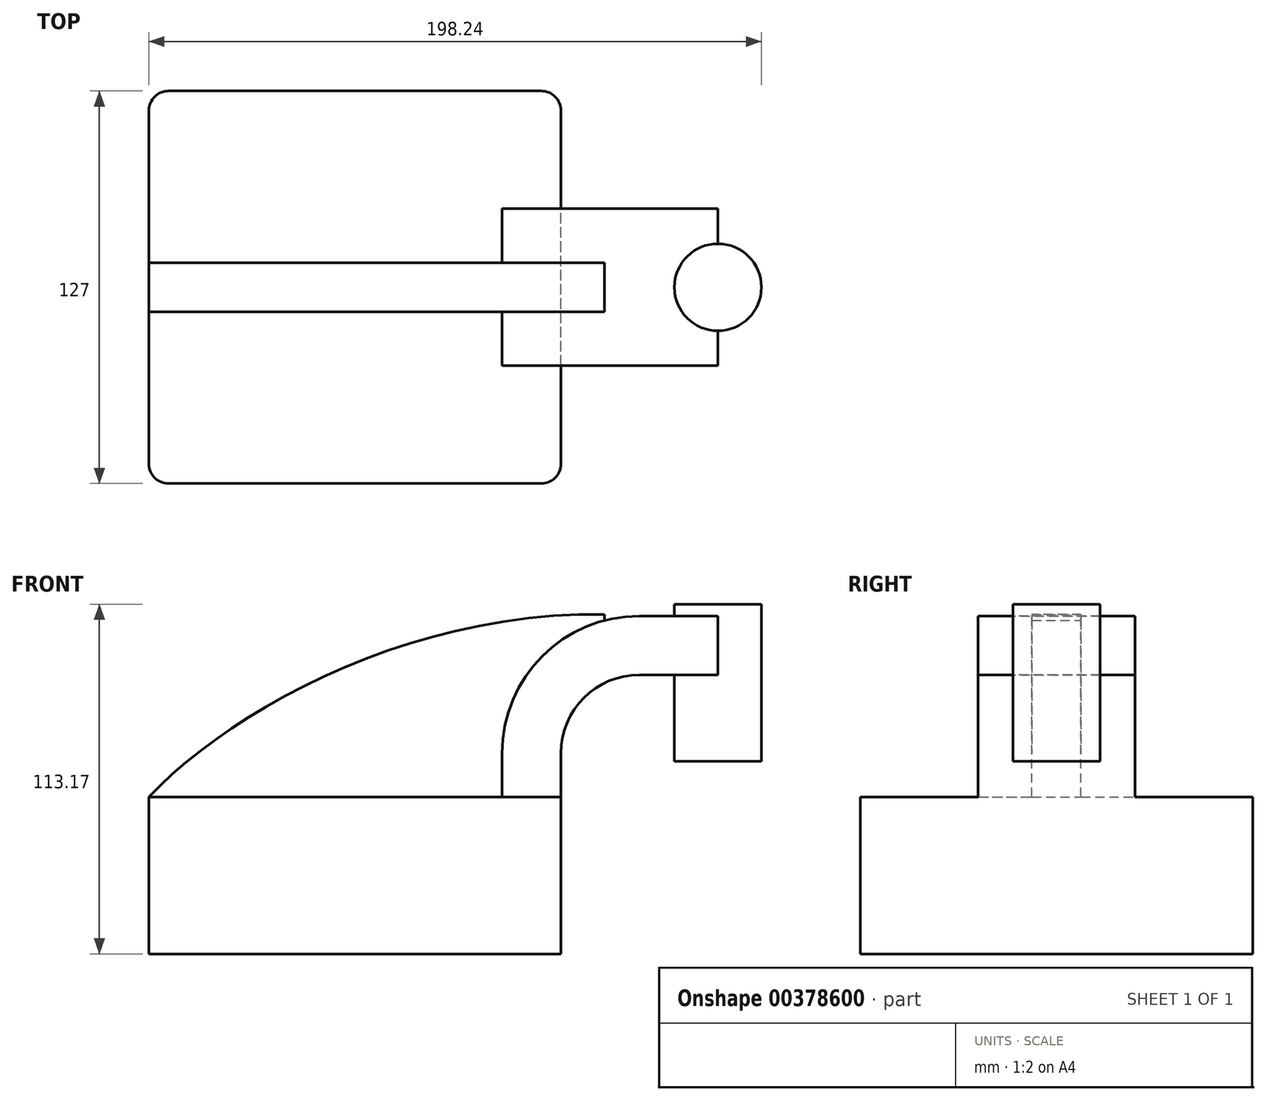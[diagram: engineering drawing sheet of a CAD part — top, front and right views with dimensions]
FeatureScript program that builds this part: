
annotation { "Feature Type Name" : "Feature", "Feature Type Description" : "" }
export const myFeature = defineFeature(function(context is Context, id is Id, definition is map)
    precondition{}
    {
        {
            var Q0;
            Q0=qCreatedBy(makeId("Front.planeOp"),FACE);
            var sketch = newSketch(context, id + "F0", { "sketchPlane" : qUnion([Q0])});
            skLineSegment(sketch, "E0.bottom", {"start": v(-66.68, -25.4) * mm, "end": v(66.67, -25.4) * mm});
            skLineSegment(sketch, "E0.top", {"start": v(-66.68, 25.4) * mm, "end": v(66.67, 25.4) * mm});
            skLineSegment(sketch, "E0.left", {"start": v(-66.68, -25.4) * mm, "end": v(-66.68, 25.4) * mm});
            skLineSegment(sketch, "E0.right", {"start": v(66.67, -25.4) * mm, "end": v(66.67, 25.4) * mm});
            skPoint(sketch, "E0.middle", {"position": v(0, 0) * mm});
            skLineSegment(sketch, "E1.bottom", {"start": v(131.56, 87.77) * mm, "end": v(80.76, 87.77) * mm});
            skLineSegment(sketch, "E1.top", {"start": v(131.56, 36.97) * mm, "end": v(80.76, 36.97) * mm});
            skLineSegment(sketch, "E1.left", {"start": v(131.56, 87.77) * mm, "end": v(131.56, 36.97) * mm});
            skLineSegment(sketch, "E1.right", {"start": v(80.76, 87.77) * mm, "end": v(80.76, 36.97) * mm});
            skLineSegment(sketch, "E2", {"start": v(66.67, 25.4) * mm, "end": v(66.67, 39.48) * mm});
            skArc(sketch, "E3", {"start": v(66.68, 39.48) * mm, "mid": v(74.11, 57.44) * mm, "end": v(92.08, 64.88) * mm});
            skLineSegment(sketch, "E4", {"start": v(92.08, 64.88) * mm, "end": v(117.48, 64.88) * mm});
            skLineSegment(sketch, "E5.0", {"start": v(92.08, 83.93) * mm, "end": v(117.48, 83.93) * mm});
            skArc(sketch, "E5.1", {"start": v(47.63, 39.48) * mm, "mid": v(60.64, 70.91) * mm, "end": v(92.08, 83.93) * mm});
            skLineSegment(sketch, "E5.2", {"start": v(47.63, 25.4) * mm, "end": v(47.63, 39.48) * mm});
            skLineSegment(sketch, "E6", {"start": v(117.48, 36.97) * mm, "end": v(117.48, 87.77) * mm});
            skFitSpline(sketch, "E7", {"points": [v(-66.68, 25.4) * mm, v(92.08, 83.93) * mm], "startDerivative": vector(85.38, 89.35) * mm, "endDerivative": vector(204.96, -15.55) * mm});
            skSolve(sketch);
        }
        {
            var Q0;
            Q0=makeQuery(id+"F0.imprint","IMPRINT",FACE,{"disambiguationData":[TD([[makeQuery(id+"F0.imprint","IMPRINT",EDGE,{"derivedFrom":sQuery(id+"F0.wireOp",EDGE,"E0.bottom")}),1.0]])]});
            extrude(context, id + "F1", {"entities" : qUnion([Q0]), "endBound" : BoundingType.SYMMETRIC, "depth" : 127 * mm});
        }
        {
            var Q0;
            {var subQ1=sQuery(id+"F0.wireOp",EDGE,"E2");Q0=makeQuery(id+"F0.imprint","IMPRINT",FACE,{"disambiguationData":[TD([[makeQuery(id+"F0.imprint","IMPRINT",EDGE,{"derivedFrom":subQ1}),1.0]])]});}
            var Q1;
            {var subQ1=sQuery(id+"F0.wireOp",EDGE,"E4");Q1=makeQuery(id+"F0.imprint","IMPRINT",FACE,{"disambiguationData":[TD([[makeQuery(id+"F0.imprint","IMPRINT",EDGE,{"derivedFrom":subQ1}),1.0]])]});}
            extrude(context, id + "F2", {"entities" : qUnion([Q0, Q1]), "operationType" : NewBodyOperationType.ADD, "endBound" : BoundingType.SYMMETRIC, "depth" : 50.8 * mm});
        }
        {
            var Q0;
            {var subQ0=sQuery(id+"F0.wireOp",EDGE,"E5.2");Q0=makeQuery(id+"F0.imprint","IMPRINT",FACE,{"disambiguationData":[TD([[makeQuery(id+"F0.imprint","IMPRINT",EDGE,{"derivedFrom":subQ0}),1.0]])]});}
            extrude(context, id + "F3", {"entities" : qUnion([Q0]), "operationType" : NewBodyOperationType.ADD, "endBound" : BoundingType.SYMMETRIC, "depth" : 15.88 * mm});
        }
        {
            var Q0;
            {var subQ0=sQuery(id+"F0.wireOp",EDGE,"E1.left");Q0=makeQuery(id+"F0.imprint","IMPRINT",FACE,{"disambiguationData":[TD([[makeQuery(id+"F0.imprint","IMPRINT",EDGE,{"derivedFrom":subQ0}),-1.0]])]});}
            var Q1;
            Q1=sQuery(id+"F0.wireOp",EDGE,"E6");
            revolve(context, id + "F4", {"operationType" : NewBodyOperationType.ADD, "entities" : qUnion([Q0]), "axis" : qUnion([Q1]), "revolveType" : RevolveType.FULL});
        }
        {
            var Q0;
            Q0=makeQuery(id+"F1.opExtrude","CAP_EDGE",EDGE,{"disambiguationData":[OSD([sQuery(id+"F0.wireOp",EDGE,"E0.left")])],"isStart":false});
            var Q1;
            Q1=makeQuery(id+"F1.opExtrude","CAP_EDGE",EDGE,{"disambiguationData":[OSD([sQuery(id+"F0.wireOp",EDGE,"E0.right")])],"isStart":false});
            var Q2;
            Q2=makeQuery(id+"F1.opExtrude","CAP_EDGE",EDGE,{"disambiguationData":[OSD([sQuery(id+"F0.wireOp",EDGE,"E0.right")])],"isStart":true});
            var Q3;
            Q3=makeQuery(id+"F1.opExtrude","CAP_EDGE",EDGE,{"disambiguationData":[OSD([sQuery(id+"F0.wireOp",EDGE,"E0.left")])],"isStart":true});
            fillet(context, id + "F5", {"entities" : qUnion([Q0, Q1, Q2, Q3]), "radius" : 6.35 * mm, "tangentPropagation" : true, "allowEdgeOverflow" : false});
        }
    });
